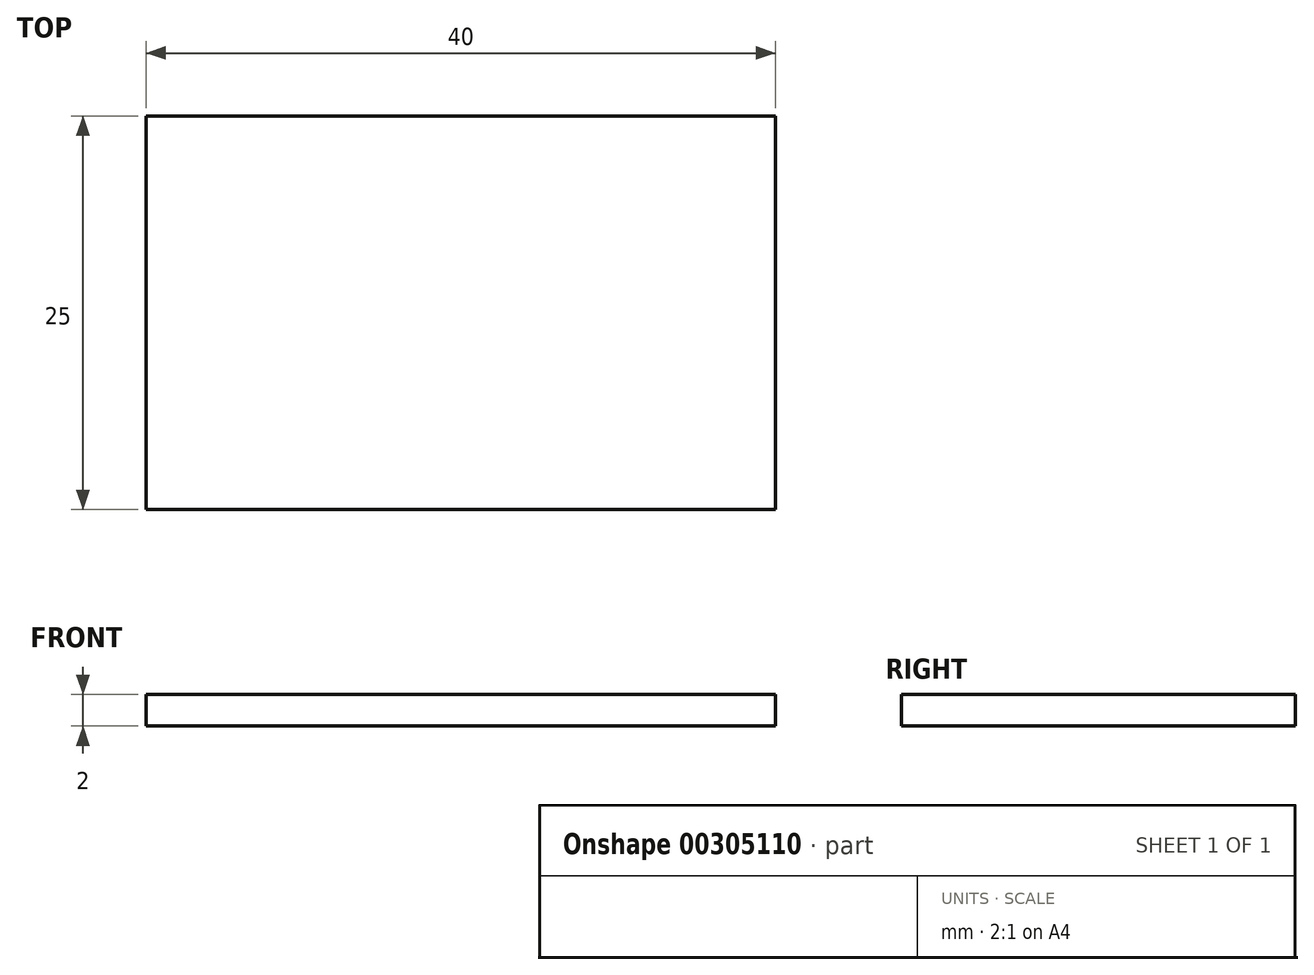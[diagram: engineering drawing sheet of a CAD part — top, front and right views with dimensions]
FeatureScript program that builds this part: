
annotation { "Feature Type Name" : "Feature", "Feature Type Description" : "" }
export const myFeature = defineFeature(function(context is Context, id is Id, definition is map)
    precondition{}
    {
        {
            var Q0;
            Q0=qCreatedBy(makeId("Top.planeOp"),FACE);
            var sketch = newSketch(context, id + "F0", { "sketchPlane" : qUnion([Q0])});
            skLineSegment(sketch, "E0.bottom", {"start": v(0, 0) * mm, "end": v(-40, 0) * mm});
            skLineSegment(sketch, "E0.top", {"start": v(0, 25) * mm, "end": v(-40, 25) * mm});
            skLineSegment(sketch, "E0.left", {"start": v(0, 0) * mm, "end": v(0, 25) * mm});
            skLineSegment(sketch, "E0.right", {"start": v(-40, 0) * mm, "end": v(-40, 25) * mm});
            skSolve(sketch);
        }
        {
            var Q0;
            Q0=makeQuery(id+"F0.imprint","IMPRINT",FACE,{"disambiguationData":[TD([[makeQuery(id+"F0.imprint","IMPRINT",EDGE,{"derivedFrom":sQuery(id+"F0.wireOp",EDGE,"E0.bottom")}),-1.0]])]});
            extrude(context, id + "F1", {"entities" : qUnion([Q0]), "depth" : 2 * mm});
        }
    });
